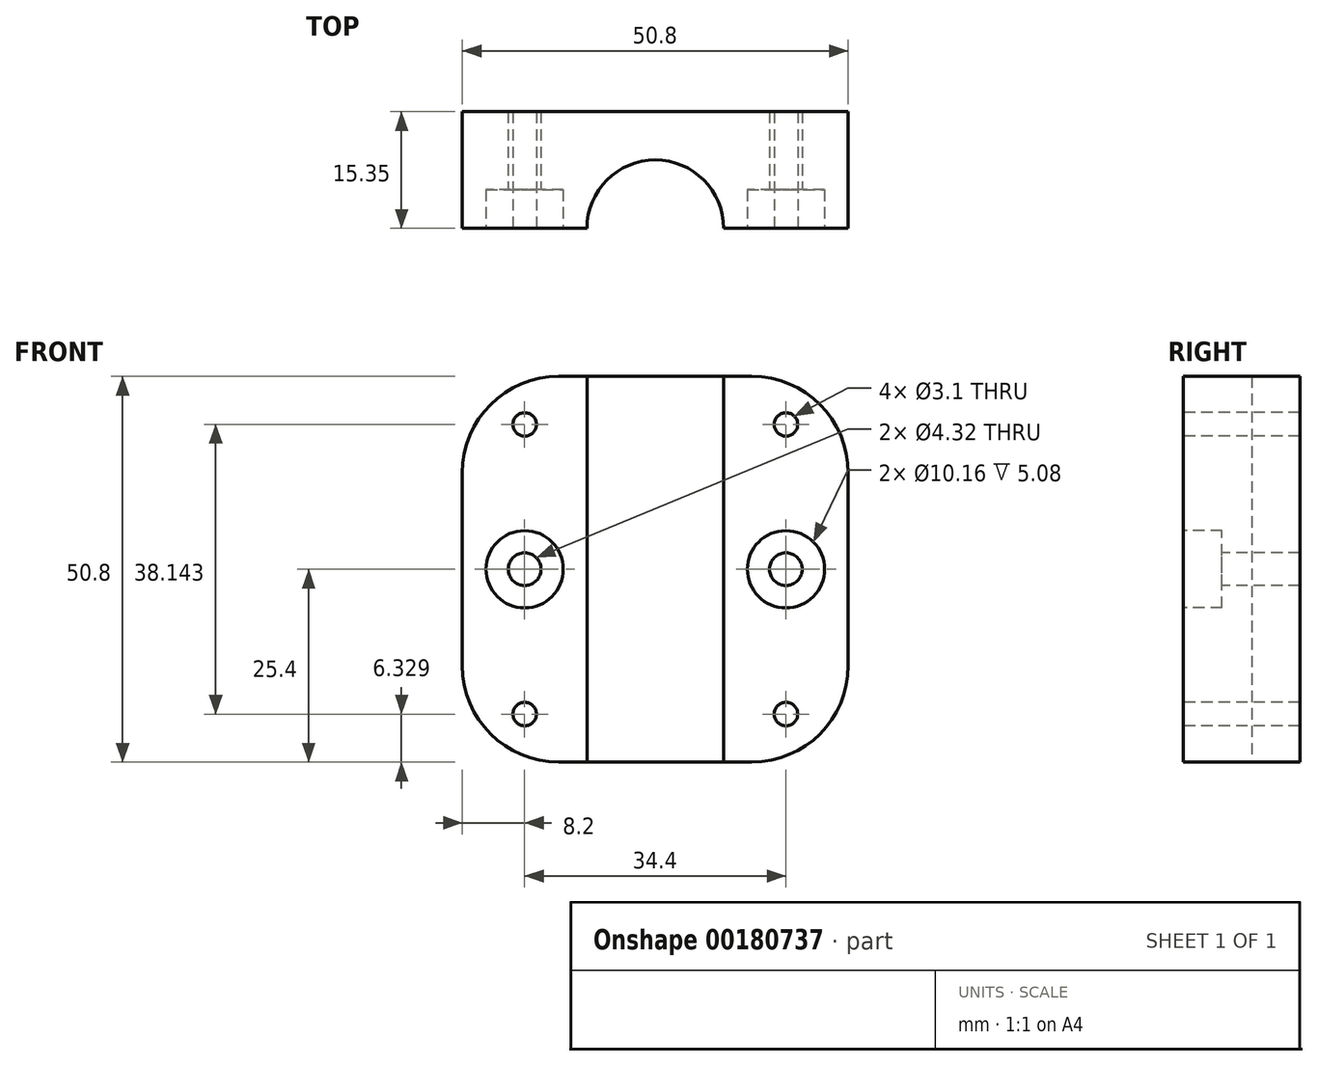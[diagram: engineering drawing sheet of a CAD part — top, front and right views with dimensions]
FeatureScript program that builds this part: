
annotation { "Feature Type Name" : "Feature", "Feature Type Description" : "" }
export const myFeature = defineFeature(function(context is Context, id is Id, definition is map)
    precondition{}
    {
        {
            var Q0;
            Q0=qCreatedBy(makeId("Top.planeOp"),FACE);
            var sketch = newSketch(context, id + "F0", { "sketchPlane" : qUnion([Q0])});
            skLineSegment(sketch, "E0.bottom", {"start": v(25.4, -25.4) * mm, "end": v(-25.4, -25.4) * mm});
            skLineSegment(sketch, "E0.top", {"start": v(25.4, 25.4) * mm, "end": v(-25.4, 25.4) * mm});
            skLineSegment(sketch, "E0.left", {"start": v(25.4, -25.4) * mm, "end": v(25.4, 25.4) * mm});
            skLineSegment(sketch, "E0.right", {"start": v(-25.4, -25.4) * mm, "end": v(-25.4, 25.4) * mm});
            skPoint(sketch, "E0.middle", {"position": v(0, 0) * mm});
            skSolve(sketch);
        }
        {
            var Q0;
            Q0=makeQuery(id+"F0.imprint","IMPRINT",FACE,{"disambiguationData":[TD([[makeQuery(id+"F0.imprint","IMPRINT",EDGE,{"derivedFrom":sQuery(id+"F0.wireOp",EDGE,"E0.bottom")}),-1.0]])]});
            extrude(context, id + "F1", {"entities" : qUnion([Q0]), "depth" : 50.8 * mm});
        }
        {
            var Q0;
            Q0=makeQuery(id+"F1.opExtrude","CAP_FACE",FACE,{"disambiguationData":[OSD([sQuery(id+"F0.wireOp",EDGE,"E0.bottom"),sQuery(id+"F0.wireOp",EDGE,"E0.top"),sQuery(id+"F0.wireOp",EDGE,"E0.left"),sQuery(id+"F0.wireOp",EDGE,"E0.right")])],"isStart":true});
            var sketch = newSketch(context, id + "F2", { "sketchPlane" : qUnion([Q0])});
            skCircle(sketch, "E1", {"center": v(0, 0) * mm, "radius": 9 * mm});
            skSolve(sketch);
        }
        {
            var Q0;
            Q0 = qSketchRegion(id + "F2", true);
            extrude(context, id + "F3", {"entities" : qUnion([Q0]), "operationType" : NewBodyOperationType.REMOVE, "oppositeDirection" : true, "depth" : 407.42 * mm});
        }
        {
            var Q0;
            Q0=makeQuery(id+"F1.opExtrude","CAP_FACE",FACE,{"disambiguationData":[OSD([sQuery(id+"F0.wireOp",EDGE,"E0.bottom"),sQuery(id+"F0.wireOp",EDGE,"E0.top"),sQuery(id+"F0.wireOp",EDGE,"E0.left"),sQuery(id+"F0.wireOp",EDGE,"E0.right")])],"isStart":true});
            var sketch = newSketch(context, id + "F4", { "sketchPlane" : qUnion([Q0])});
            skLineSegment(sketch, "E2.bottom", {"start": v(-25.4, 25.4) * mm, "end": v(34.72, 25.4) * mm});
            skLineSegment(sketch, "E2.top", {"start": v(-25.4, 0) * mm, "end": v(34.72, 0) * mm});
            skLineSegment(sketch, "E2.left", {"start": v(-25.4, 25.4) * mm, "end": v(-25.4, 0) * mm});
            skLineSegment(sketch, "E2.right", {"start": v(34.72, 25.4) * mm, "end": v(34.72, 0) * mm});
            skSolve(sketch);
        }
        {
            var Q0;
            Q0 = qSketchRegion(id + "F4", true);
            extrude(context, id + "F5", {"entities" : qUnion([Q0]), "operationType" : NewBodyOperationType.REMOVE, "oppositeDirection" : true, "depth" : 338.58 * mm});
        }
        {
            var Q0;
            {var subQ0=sQuery(id+"F0.wireOp",EDGE,"E0.right");Q0=makeQuery(id+"F5.boolean.opBoolean","COPY",FACE,{"disambiguationData":[TD([makeQuery(id+"F1.opExtrude","SWEPT_FACE",FACE,{"disambiguationData":[OSD([subQ0])]})])],"derivedFrom":makeQuery(id+"F5.opExtrude","SWEPT_FACE",FACE,{"disambiguationData":[OSD([sQuery(id+"F4.wireOp",EDGE,"E2.top")])]})});}
            var sketch = newSketch(context, id + "F6", { "sketchPlane" : qUnion([Q0])});
            skCircle(sketch, "E3", {"center": v(-17.2, 25.4) * mm, "radius": 5.08 * mm});
            skSolve(sketch);
        }
        {
            var Q0;
            Q0 = qSketchRegion(id + "F6", true);
            extrude(context, id + "F7", {"entities" : qUnion([Q0]), "operationType" : NewBodyOperationType.REMOVE, "oppositeDirection" : true, "depth" : 5.08 * mm});
        }
        {
            var Q0;
            Q0=makeQuery(id+"F7.boolean.opBoolean","COPY",FACE,{"derivedFrom":makeQuery(id+"F7.opExtrude","CAP_FACE",FACE,{"disambiguationData":[OSD([sQuery(id+"F6.wireOp",EDGE,"E3")])],"isStart":false})});
            var sketch = newSketch(context, id + "F8", { "sketchPlane" : qUnion([Q0])});
            skCircle(sketch, "E4", {"center": v(-17.2, 25.4) * mm, "radius": 2.16 * mm});
            skSolve(sketch);
        }
        {
            var Q0;
            Q0 = qSketchRegion(id + "F8", true);
            extrude(context, id + "F9", {"entities" : qUnion([Q0]), "operationType" : NewBodyOperationType.REMOVE, "oppositeDirection" : true, "depth" : 25.4 * mm});
        }
        {
            var Q0;
            {var subQ0=sQuery(id+"F0.wireOp",EDGE,"E0.right");Q0=makeQuery(id+"F5.boolean.opBoolean","COPY",FACE,{"disambiguationData":[TD([makeQuery(id+"F1.opExtrude","SWEPT_FACE",FACE,{"disambiguationData":[OSD([subQ0])]})])],"derivedFrom":makeQuery(id+"F5.opExtrude","SWEPT_FACE",FACE,{"disambiguationData":[OSD([sQuery(id+"F4.wireOp",EDGE,"E2.top")])]})});}
            var sketch = newSketch(context, id + "F10", { "sketchPlane" : qUnion([Q0])});
            skCircle(sketch, "E5", {"center": v(-17.2, 44.47) * mm, "radius": 1.55 * mm});
            skPoint(sketch, "E5.centerSnap0", {"position": v(-17.2, 50.8) * mm});
            skSolve(sketch);
        }
        {
            var Q0;
            Q0 = qSketchRegion(id + "F10", true);
            extrude(context, id + "F11", {"entities" : qUnion([Q0]), "operationType" : NewBodyOperationType.REMOVE, "oppositeDirection" : true, "depth" : 25.4 * mm});
        }
        {
            var Q0;
            {var subQ0=sQuery(id+"F0.wireOp",EDGE,"E0.right");Q0=makeQuery(id+"F5.boolean.opBoolean","COPY",FACE,{"disambiguationData":[TD([makeQuery(id+"F1.opExtrude","SWEPT_FACE",FACE,{"disambiguationData":[OSD([subQ0])]})])],"derivedFrom":makeQuery(id+"F5.opExtrude","SWEPT_FACE",FACE,{"disambiguationData":[OSD([sQuery(id+"F4.wireOp",EDGE,"E2.top")])]})});}
            var sketch = newSketch(context, id + "F12", { "sketchPlane" : qUnion([Q0])});
            skCircle(sketch, "E6.MirrorC", {"center": v(17.2, 44.47) * mm, "radius": 1.55 * mm});
            skCircle(sketch, "E7.MirrorC", {"center": v(17.2, 25.4) * mm, "radius": 5.08 * mm, "construction": true});
            skCircle(sketch, "E8.MirrorC", {"center": v(17.2, 25.4) * mm, "radius": 2.16 * mm});
            skSolve(sketch);
        }
        {
            var Q0;
            Q0 = qSketchRegion(id + "F12", true);
            extrude(context, id + "F13", {"entities" : qUnion([Q0]), "operationType" : NewBodyOperationType.REMOVE, "oppositeDirection" : true, "depth" : 25.4 * mm});
        }
        {
            var Q0;
            {var subQ1=sQuery(id+"F0.wireOp",EDGE,"E0.left");Q0=makeQuery(id+"F5.boolean.opBoolean","COPY",FACE,{"disambiguationData":[TD([makeQuery(id+"F1.opExtrude","SWEPT_FACE",FACE,{"disambiguationData":[OSD([subQ1])]})])],"derivedFrom":makeQuery(id+"F5.opExtrude","SWEPT_FACE",FACE,{"disambiguationData":[OSD([sQuery(id+"F4.wireOp",EDGE,"E2.top")])]})});}
            var sketch = newSketch(context, id + "F14", { "sketchPlane" : qUnion([Q0])});
            skCircle(sketch, "E9.MirrorC", {"center": v(17.2, 25.4) * mm, "radius": 5.08 * mm});
            skSolve(sketch);
        }
        {
            var Q0;
            Q0 = qSketchRegion(id + "F14", true);
            extrude(context, id + "F15", {"entities" : qUnion([Q0]), "operationType" : NewBodyOperationType.REMOVE, "oppositeDirection" : true, "depth" : 5.08 * mm});
        }
        {
            var Q0;
            Q0=makeQuery(id+"F1.opExtrude","CAP_FACE",FACE,{"disambiguationData":[OSD([sQuery(id+"F0.wireOp",EDGE,"E0.bottom"),sQuery(id+"F0.wireOp",EDGE,"E0.top"),sQuery(id+"F0.wireOp",EDGE,"E0.left"),sQuery(id+"F0.wireOp",EDGE,"E0.right")])],"isStart":false});
            cPlane(context, id + "F16", {"entities" : qUnion([Q0]), "cplaneType" : CPlaneType.OFFSET, "offset" : 25.4 * mm, "oppositeDirection" : true, "width" : 152.4 * mm, "height" : 152.4 * mm});
        }
        {
            var Q0;
            Q0=makeQuery(id+"F1.opExtrude","SWEPT_BODY",BODY,{"disambiguationData":[OSD([sQuery(id+"F0.wireOp",EDGE,"E0.bottom"),sQuery(id+"F0.wireOp",EDGE,"E0.top"),sQuery(id+"F0.wireOp",EDGE,"E0.left"),sQuery(id+"F0.wireOp",EDGE,"E0.right")])]});
            var Q1;
            Q1=qCreatedBy(id+"F16.planeOp",FACE);
            mirror(context, id + "F17", {"operationType" : NewBodyOperationType.INTERSECT, "entities" : qUnion([Q0]), "mirrorPlane" : qUnion([Q1])});
        }
        {
            var Q0;
            Q0=makeQuery(id+"F1.opExtrude","CAP_EDGE",EDGE,{"disambiguationData":[OSD([sQuery(id+"F0.wireOp",EDGE,"E0.right")])],"isStart":true});
            var Q1;
            Q1=makeQuery(id+"F1.opExtrude","CAP_EDGE",EDGE,{"disambiguationData":[OSD([sQuery(id+"F0.wireOp",EDGE,"E0.right")])],"isStart":false});
            var Q2;
            Q2=makeQuery(id+"F1.opExtrude","CAP_EDGE",EDGE,{"disambiguationData":[OSD([sQuery(id+"F0.wireOp",EDGE,"E0.left")])],"isStart":true});
            var Q3;
            Q3=makeQuery(id+"F1.opExtrude","CAP_EDGE",EDGE,{"disambiguationData":[OSD([sQuery(id+"F0.wireOp",EDGE,"E0.left")])],"isStart":false});
            fillet(context, id + "F18", {"entities" : qUnion([Q0, Q1, Q2, Q3]), "radius" : 12.7 * mm, "tangentPropagation" : true, "allowEdgeOverflow" : false});
        }
        {
            var Q0;
            Q0=makeQuery(id+"F1.opExtrude","CAP_FACE",FACE,{"disambiguationData":[OSD([sQuery(id+"F0.wireOp",EDGE,"E0.bottom"),sQuery(id+"F0.wireOp",EDGE,"E0.top"),sQuery(id+"F0.wireOp",EDGE,"E0.left"),sQuery(id+"F0.wireOp",EDGE,"E0.right")])],"isStart":true});
            var sketch = newSketch(context, id + "F19", { "sketchPlane" : qUnion([Q0])});
            skLineSegment(sketch, "E10", {"start": v(0, -9) * mm, "end": v(0, -15.35) * mm});
            skLineSegment(sketch, "E11", {"start": v(0, -15.35) * mm, "end": v(-44.71, -15.35) * mm});
            skLineSegment(sketch, "E12", {"start": v(-44.71, -15.35) * mm, "end": v(-42.65, -31.93) * mm});
            skLineSegment(sketch, "E13", {"start": v(-42.65, -31.93) * mm, "end": v(43.38, -33.96) * mm});
            skLineSegment(sketch, "E14", {"start": v(0, -15.35) * mm, "end": v(37.31, -15.35) * mm});
            skLineSegment(sketch, "E15", {"start": v(37.31, -15.35) * mm, "end": v(43.38, -33.96) * mm});
            skSolve(sketch);
        }
        {
            var Q0;
            Q0 = qSketchRegion(id + "F19", true);
            extrude(context, id + "F20", {"entities" : qUnion([Q0]), "operationType" : NewBodyOperationType.REMOVE, "oppositeDirection" : true, "depth" : 72.39 * mm});
        }
    });
